# Revit family: Haworth_Planes_ConferenceTable_HexagonTwoPiece
name_source: partatom
category: Furniture Systems
revit_build: Autodesk Revit 2018 (Build: 20170223_1515(x64)
units: mm (PartAtom-declared; Revit-internal decimal feet)

## family parameters
Always vertical = Yes
Cut with Voids When Loaded = No
OmniClass Number = 23.40.70.14.64.21
OmniClass Title = Systems Furniture
Part Type = Normal
Room Calculation Point = No
Round Connector Dimension = Use Diameter
Shared = No
Work Plane-Based = No

## types (1)
- 180w 60d
    Actual Depth = 60"
    Actual Height = 29"
    Actual Width = 180"
    Assembly Code = E2020200
    Cable Base = Yes
    Custom Size = No
    Cutout = Yes
    Cutout Center Offset = 45"
    Cutout Depth = 4"
    Cutout Side Offset = 22 1/2"
    Cutout Width = 8"
    Depth = 60"
    Description = Haworth - Planes - Conference Table Hexagon - Two-Piece
    Edgeband = Yes
    Flip Top = Yes
    Flip Top Finish = Haworth _ Paint _ Metallic Champagne
    Fliptop Center Vis. = Yes
    Fliptop Depth = 4 3/8"
    Fliptop Side Vis. = No
    Fliptop Width = 8 1/4"
    Half Width = 90"
    Knife Edge = No
    Manufacturer = Haworth
    Max. Depth = 60"
    Max. Height = 29"
    Max. Width = 180"
    Middle Leg_Interior = Yes
    Min. Depth = 42"
    Min. Height = 29"
    Min. Width = 126"
    Min/Max Width = 126-180 @ 6 in. increments
    Model = TARX
    No Cable Base = No
    Opening Center = Yes
    Opening Double = No
    Opening Double Wide = No
    Opening Left/Right = No
    Opening Single = Yes
    Opening Single Wide = No
    Revision Number = 1
    Size = Verify Final Dim. w/ Haworth
    Standard Depths = 42, 48, 54, 60 in.
    Standard Height = 29 in.
    Support Height = 27 13/16"
    Support Location_Front_Back = 6 11/16"
    Support Location_Middle = 40"
    Support Location_Side = 8 1/16"
    Sustainability Info = http://media.haworth.com
    Table Thickness = 1 3/16"
    URL = www.haworth.com
    URL - Product = http://www.haworth.com
    Warranty = http://www.haworth.com
    Width = 180"

## geometry (parser evidence)
native form markers: Sweep x10
no freeform markers — native parametric forms only
